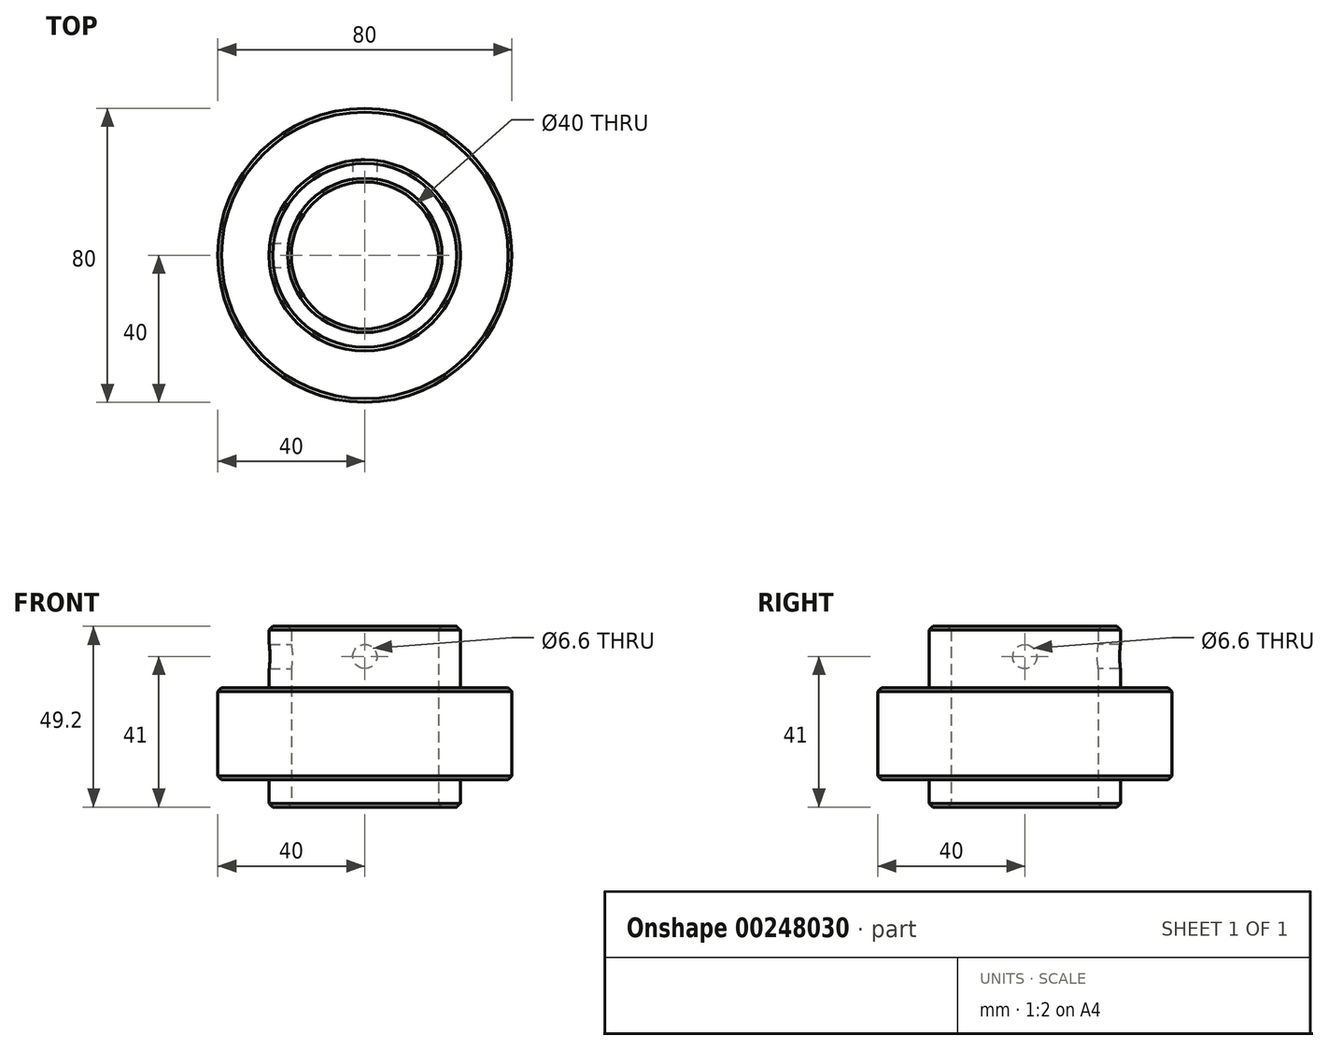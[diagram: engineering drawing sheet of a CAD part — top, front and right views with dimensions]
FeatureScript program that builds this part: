
annotation { "Feature Type Name" : "Feature", "Feature Type Description" : "" }
export const myFeature = defineFeature(function(context is Context, id is Id, definition is map)
    precondition{}
    {
        {
            var Q0;
            Q0=qCreatedBy(makeId("Top.planeOp"),FACE);
            var sketch = newSketch(context, id + "F0", { "sketchPlane" : qUnion([Q0])});
            skCircle(sketch, "E0", {"center": v(0, 0) * mm, "radius": 26 * mm});
            skCircle(sketch, "E1", {"center": v(0, 0) * mm, "radius": 20 * mm});
            skSolve(sketch);
        }
        {
            var Q0;
            Q0=makeQuery(id+"F0.imprint","IMPRINT",FACE,{"disambiguationData":[TD([[makeQuery(id+"F0.imprint","IMPRINT",EDGE,{"derivedFrom":sQuery(id+"F0.wireOp",EDGE,"E0")}),1.0]])]});
            extrude(context, id + "F1", {"entities" : qUnion([Q0]), "depth" : 29.2 * mm, "hasSecondDirection" : true, "secondDirectionOppositeDirection" : true, "secondDirectionDepth" : 20 * mm});
        }
        {
            var Q0;
            Q0=makeQuery(id+"F1.opExtrude","CAP_EDGE",EDGE,{"disambiguationData":[OSD([sQuery(id+"F0.wireOp",EDGE,"E1")])],"isStart":false});
            var Q1;
            Q1=makeQuery(id+"F1.opExtrude","CAP_EDGE",EDGE,{"disambiguationData":[OSD([sQuery(id+"F0.wireOp",EDGE,"E0")])],"isStart":false});
            var Q2;
            Q2=makeQuery(id+"F1.opExtrude","CAP_EDGE",EDGE,{"disambiguationData":[OSD([sQuery(id+"F0.wireOp",EDGE,"E1")])],"isStart":true});
            var Q3;
            Q3=makeQuery(id+"F1.opExtrude","CAP_EDGE",EDGE,{"disambiguationData":[OSD([sQuery(id+"F0.wireOp",EDGE,"E0")])],"isStart":true});
            chamfer(context, id + "F2", {"entities" : qUnion([Q0, Q1, Q2, Q3]), "width" : 1 * mm, "tangentPropagation" : true});
        }
        {
            var Q0;
            Q0=qCreatedBy(makeId("Front.planeOp"),FACE);
            var sketch = newSketch(context, id + "F3", { "sketchPlane" : qUnion([Q0])});
            skPoint(sketch, "E2", {"position": v(0, 21) * mm});
            skSolve(sketch);
        }
        {
            var Q0;
            Q0=sQuery(id+"F3.wireOp",VERTEX,"E2");
            var Q1;
            Q1=makeQuery(id+"F1.opExtrude","SWEPT_BODY",BODY,{"disambiguationData":[OSD([sQuery(id+"F0.wireOp",EDGE,"E0"),sQuery(id+"F0.wireOp",EDGE,"E1")])]});
            hole(context, id + "F4", {"style" : HoleStyle.SIMPLE, "endStyle" : HoleEndStyle.THROUGH, "standardTappedOrClearance" : lookupTablePath({ "standard" : "ISO", "fit" : "Normal", "size" : "M6", "type" : "Clearance" }), "standardBlindInLast" : lookupTablePath({ "fit" : "Standard", "standard" : "ISO", "size" : "M6", "type" : "Clearance" }), "holeDiameter" : 6.6 * mm, "tappedDepth" : 12 * mm, "tapClearance" : 3, "locations" : qUnion([Q0]), "scope" : qUnion([Q1])});
        }
        {
            var Q0;
            Q0=qCreatedBy(makeId("Right.planeOp"),FACE);
            var sketch = newSketch(context, id + "F5", { "sketchPlane" : qUnion([Q0])});
            skPoint(sketch, "E3", {"position": v(0, 0) * mm});
            skPoint(sketch, "E4", {"position": v(0, 21) * mm});
            skSolve(sketch);
        }
        {
            var Q0;
            Q0=sQuery(id+"F5.wireOp",VERTEX,"E4");
            var Q1;
            Q1=makeQuery(id+"F1.opExtrude","SWEPT_BODY",BODY,{"disambiguationData":[OSD([sQuery(id+"F0.wireOp",EDGE,"E0"),sQuery(id+"F0.wireOp",EDGE,"E1")])]});
            hole(context, id + "F6", {"style" : HoleStyle.SIMPLE, "endStyle" : HoleEndStyle.THROUGH, "standardTappedOrClearance" : lookupTablePath({ "standard" : "ISO", "fit" : "Normal", "size" : "M6", "type" : "Clearance" }), "standardBlindInLast" : lookupTablePath({ "fit" : "Standard", "standard" : "ISO", "size" : "M6", "type" : "Clearance" }), "holeDiameter" : 6.6 * mm, "tappedDepth" : 12 * mm, "tapClearance" : 3, "locations" : qUnion([Q0]), "scope" : qUnion([Q1])});
        }
        {
            var Q0;
            Q0=qCreatedBy(makeId("Top.planeOp"),FACE);
            var sketch = newSketch(context, id + "F7", { "sketchPlane" : qUnion([Q0])});
            skCircle(sketch, "E5", {"center": v(0, 0) * mm, "radius": 40 * mm});
            skSolve(sketch);
        }
        {
            var Q0;
            Q0=makeQuery(id+"F7.imprint","IMPRINT",FACE,{"disambiguationData":[TD([[makeQuery(id+"F7.imprint","IMPRINT",EDGE,{"derivedFrom":sQuery(id+"F7.wireOp",EDGE,"E5")}),1.0]])]});
            extrude(context, id + "F8", {"entities" : qUnion([Q0]), "operationType" : NewBodyOperationType.ADD, "depth" : 12.5 * mm, "hasSecondDirection" : true, "secondDirectionOppositeDirection" : true, "secondDirectionDepth" : 12.5 * mm});
        }
        {
            var Q0;
            Q0=makeQuery(id+"F8.boolean.opBoolean","SPLIT",FACE,{"disambiguationData":[TD([makeQuery(id+"F1.opExtrude","SWEPT_FACE",FACE,{"disambiguationData":[OSD([sQuery(id+"F0.wireOp",EDGE,"E1")])]})])],"derivedFrom":makeQuery(id+"F8.opExtrude","CAP_FACE",FACE,{"disambiguationData":[OSD([sQuery(id+"F7.wireOp",EDGE,"E5")])],"isStart":false})});
            extrude(context, id + "F9", {"entities" : qUnion([Q0]), "operationType" : NewBodyOperationType.REMOVE, "oppositeDirection" : true, "depth" : 25 * mm});
        }
        {
            var Q0;
            Q0=makeQuery(id+"F8.opExtrude","CAP_EDGE",EDGE,{"disambiguationData":[OSD([sQuery(id+"F7.wireOp",EDGE,"E5")])],"isStart":false});
            var Q1;
            Q1=makeQuery(id+"F8.opExtrude","CAP_EDGE",EDGE,{"disambiguationData":[OSD([sQuery(id+"F7.wireOp",EDGE,"E5")])],"isStart":true});
            chamfer(context, id + "F10", {"entities" : qUnion([Q0, Q1]), "width" : 1 * mm, "tangentPropagation" : true});
        }
    });
